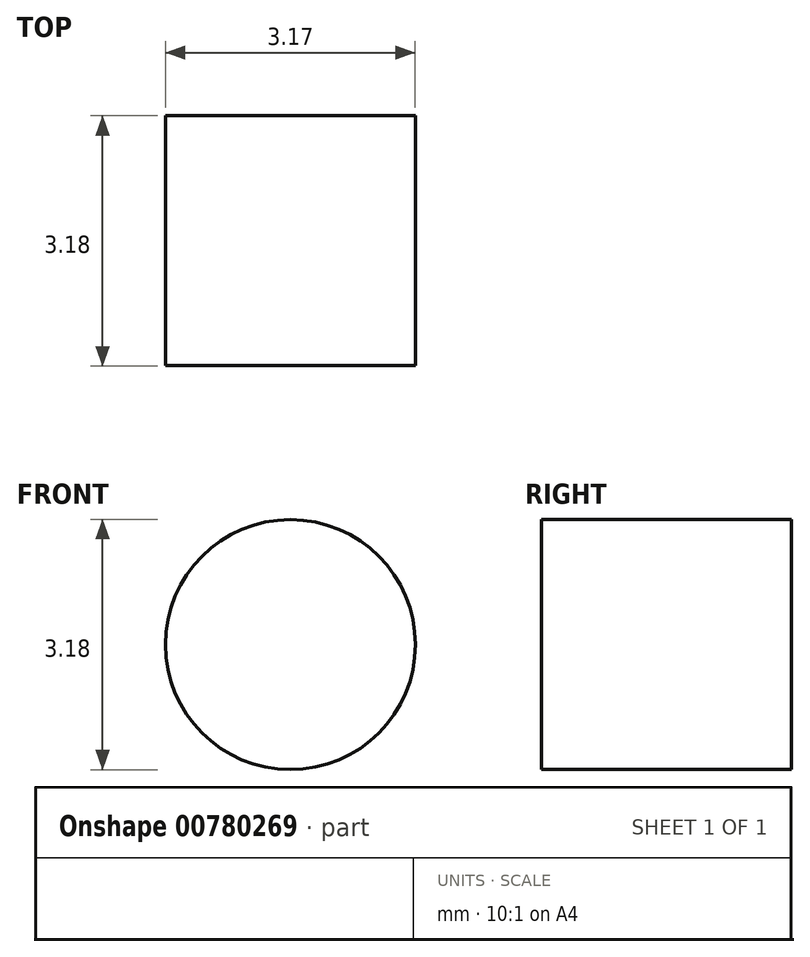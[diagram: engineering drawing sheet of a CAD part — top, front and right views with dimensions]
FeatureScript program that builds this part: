
annotation { "Feature Type Name" : "Feature", "Feature Type Description" : "" }
export const myFeature = defineFeature(function(context is Context, id is Id, definition is map)
    precondition{}
    {
        {
            var Q0;
            Q0=qCreatedBy(makeId("Front.planeOp"),FACE);
            var sketch = newSketch(context, id + "F0", { "sketchPlane" : qUnion([Q0])});
            skCircle(sketch, "E0", {"center": v(-197.66, -39.84) * mm, "radius": 1.59 * mm});
            skSolve(sketch);
        }
        {
            var Q0;
            Q0 = qSketchRegion(id + "F0", true);
            extrude(context, id + "F1", {"entities" : qUnion([Q0]), "depth" : 3.17 * mm, "offsetDistance" : 25 * mm});
        }
    });
